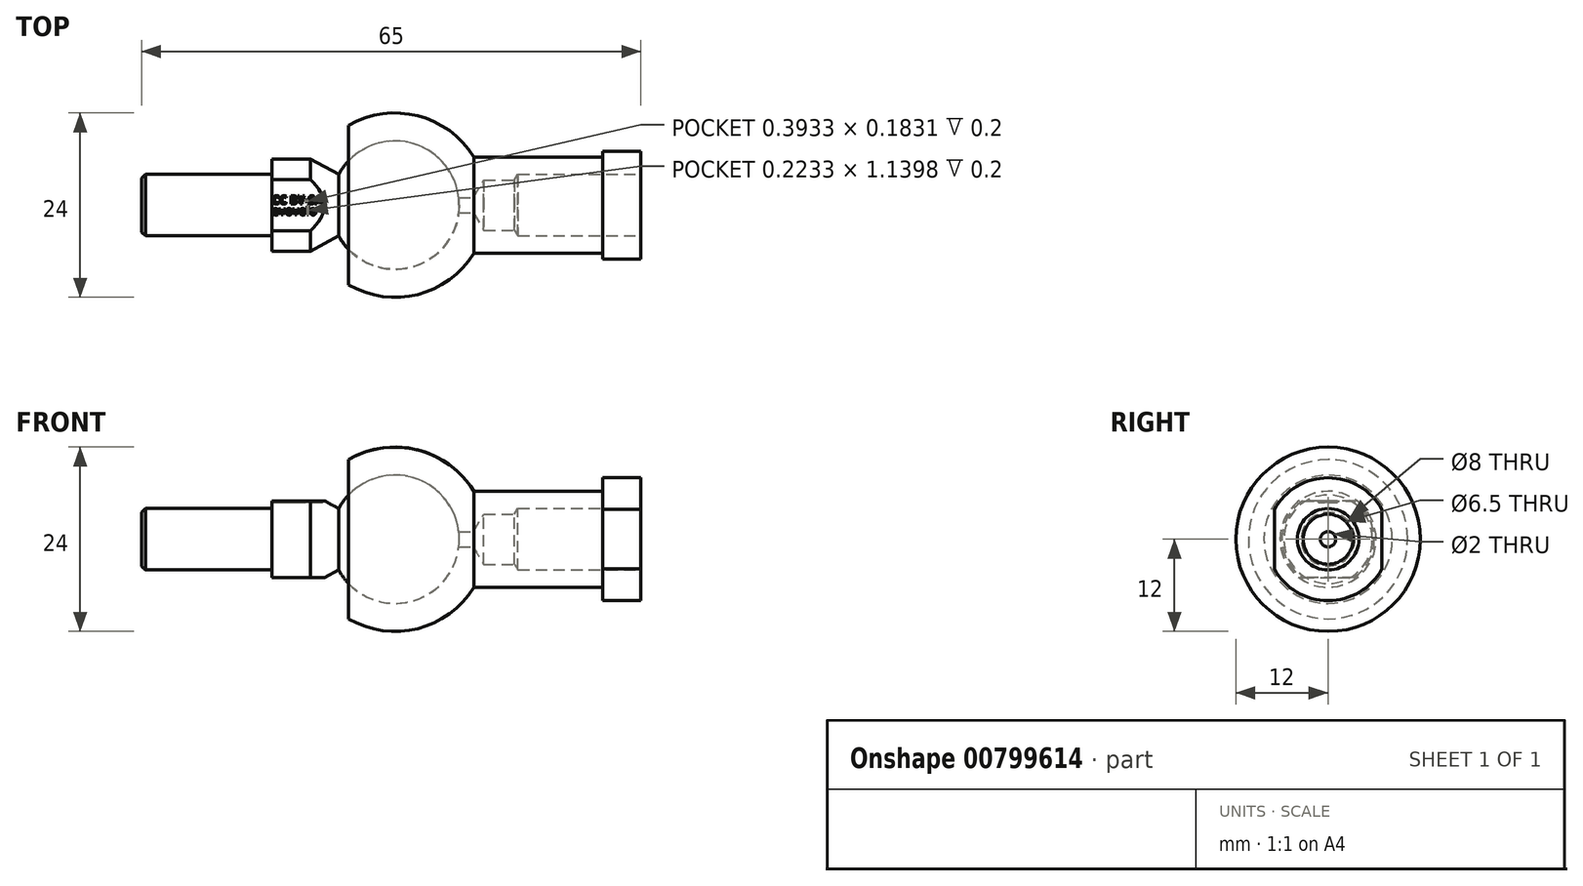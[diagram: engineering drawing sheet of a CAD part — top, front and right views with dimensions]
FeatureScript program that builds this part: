
annotation { "Feature Type Name" : "Feature", "Feature Type Description" : "" }
export const myFeature = defineFeature(function(context is Context, id is Id, definition is map)
    precondition{}
    {
        {
            var Q0;
            Q0=qCreatedBy(makeId("Top.planeOp"),FACE);
            var sketch = newSketch(context, id + "F0", { "sketchPlane" : qUnion([Q0])});
            skArc(sketch, "E0", {"start": v(8.35, 0) * mm, "mid": v(2.06, 8.1) * mm, "end": v(-7.33, 4) * mm});
            skArc(sketch, "E1", {"start": v(10.24, 6.25) * mm, "mid": v(2.94, 11.63) * mm, "end": v(-6.04, 10.37) * mm});
            skLineSegment(sketch, "E2", {"start": v(-42.01, 0) * mm, "end": v(52.59, 0) * mm, "construction": true});
            skLineSegment(sketch, "E3", {"start": v(10.24, 6.25) * mm, "end": v(27, 6.25) * mm});
            skLineSegment(sketch, "E4", {"start": v(27, 6.25) * mm, "end": v(27, 8) * mm});
            skLineSegment(sketch, "E5", {"start": v(27, 8) * mm, "end": v(32, 8) * mm});
            skLineSegment(sketch, "E6", {"start": v(32, 8) * mm, "end": v(32, 0) * mm});
            skLineSegment(sketch, "E7", {"start": v(32, 0) * mm, "end": v(8.35, 0) * mm});
            skLineSegment(sketch, "E8", {"start": v(0, 0) * mm, "end": v(-7.33, 4) * mm, "construction": true});
            skLineSegment(sketch, "E9", {"start": v(0, 0) * mm, "end": v(-6.04, 5.76) * mm, "construction": true});
            skLineSegment(sketch, "E10", {"start": v(-6.04, 10.37) * mm, "end": v(-6.04, 5.76) * mm});
            skLineSegment(sketch, "E11", {"start": v(0, 23.03) * mm, "end": v(0, -15.14) * mm, "construction": true});
            skLineSegment(sketch, "E12", {"start": v(-7.33, 4) * mm, "end": v(-11, 6) * mm});
            skLineSegment(sketch, "E13", {"start": v(-11, 6) * mm, "end": v(-16, 6) * mm});
            skLineSegment(sketch, "E14", {"start": v(-16, 6) * mm, "end": v(-16, 4) * mm});
            skLineSegment(sketch, "E15", {"start": v(-16, 4) * mm, "end": v(-33, 4) * mm});
            skLineSegment(sketch, "E16", {"start": v(-33, 4) * mm, "end": v(-33, 0) * mm});
            skLineSegment(sketch, "E17", {"start": v(-33, 0) * mm, "end": v(8.35, 0) * mm});
            skSolve(sketch);
        }
        {
            var Q0;
            Q0=makeQuery(id+"F0.imprint","IMPRINT",FACE,{"disambiguationData":[TD([[makeQuery(id+"F0.imprint","IMPRINT",EDGE,{"derivedFrom":sQuery(id+"F0.wireOp",EDGE,"E1")}),1.0]])]});
            var Q1;
            Q1=sQuery(id+"F0.wireOp",EDGE,"E2");
            revolve(context, id + "F1", {"entities" : qUnion([Q0]), "axis" : qUnion([Q1]), "revolveType" : RevolveType.FULL});
        }
        {
            var Q0;
            {var subQ1=sQuery(id+"F0.wireOp",EDGE,"E12");Q0=makeQuery(id+"F0.imprint","IMPRINT",FACE,{"disambiguationData":[TD([[makeQuery(id+"F0.imprint","IMPRINT",EDGE,{"derivedFrom":subQ1}),1.0]])]});}
            var Q1;
            Q1=sQuery(id+"F0.wireOp",EDGE,"E2");
            revolve(context, id + "F2", {"entities" : qUnion([Q0]), "axis" : qUnion([Q1]), "revolveType" : RevolveType.FULL});
        }
        {
            var Q0;
            Q0=makeQuery(id+"F1.opRevolve","SWEPT_FACE",FACE,{"disambiguationData":[OSD([sQuery(id+"F0.wireOp",EDGE,"E6")])]});
            var sketch = newSketch(context, id + "F3", { "sketchPlane" : qUnion([Q0])});
            skPoint(sketch, "E18", {"position": v(0, 0) * mm});
            skLineSegment(sketch, "E19", {"start": v(-7, 3.87) * mm, "end": v(-7, -3.87) * mm});
            skLineSegment(sketch, "E20", {"start": v(0, 12.06) * mm, "end": v(0, -11.37) * mm, "construction": true});
            skLineSegment(sketch, "E21.MirrorCS", {"start": v(7, 3.87) * mm, "end": v(7, -3.87) * mm});
            skSolve(sketch);
        }
        {
            var Q0;
            {var subQ1=sQuery(id+"F3.wireOp",EDGE,"E21.MirrorCS");Q0=makeQuery(id+"F3.imprint","IMPRINT",FACE,{"disambiguationData":[TD([[makeQuery(id+"F3.imprint","IMPRINT",EDGE,{"derivedFrom":subQ1}),1.0]])]});}
            var Q1;
            {var subQ1=sQuery(id+"F3.wireOp",EDGE,"E19");Q1=makeQuery(id+"F3.imprint","IMPRINT",FACE,{"disambiguationData":[TD([[makeQuery(id+"F3.imprint","IMPRINT",EDGE,{"derivedFrom":subQ1}),-1.0]])]});}
            extrude(context, id + "F4", {"entities" : qUnion([Q0, Q1]), "operationType" : NewBodyOperationType.REMOVE, "endBound" : BoundingType.UP_TO_NEXT, "oppositeDirection" : true, "depth" : 10 * mm});
        }
        {
            var Q0;
            Q0=sQuery(id+"F3.wireOp",VERTEX,"E18");
            var Q1;
            Q1=makeQuery(id+"F1.opRevolve","SWEPT_BODY",BODY,{"disambiguationData":[OSD([sQuery(id+"F0.wireOp",EDGE,"E0"),sQuery(id+"F0.wireOp",EDGE,"E1"),sQuery(id+"F0.wireOp",EDGE,"E3"),sQuery(id+"F0.wireOp",EDGE,"E4"),sQuery(id+"F0.wireOp",EDGE,"E5"),sQuery(id+"F0.wireOp",EDGE,"E6"),sQuery(id+"F0.wireOp",EDGE,"E7"),sQuery(id+"F0.wireOp",EDGE,"E10")])]});
            hole(context, id + "F5", {"style" : HoleStyle.SIMPLE, "holeDiameter" : 8 * mm, "endStyle" : HoleEndStyle.BLIND, "holeDepth" : 16 * mm, "locations" : qUnion([Q0]), "scope" : qUnion([Q1])});
        }
        {
            var Q0;
            Q0=sQuery(id+"F3.wireOp",VERTEX,"E18");
            var Q1;
            Q1=makeQuery(id+"F1.opRevolve","SWEPT_BODY",BODY,{"disambiguationData":[OSD([sQuery(id+"F0.wireOp",EDGE,"E0"),sQuery(id+"F0.wireOp",EDGE,"E1"),sQuery(id+"F0.wireOp",EDGE,"E3"),sQuery(id+"F0.wireOp",EDGE,"E4"),sQuery(id+"F0.wireOp",EDGE,"E5"),sQuery(id+"F0.wireOp",EDGE,"E6"),sQuery(id+"F0.wireOp",EDGE,"E7"),sQuery(id+"F0.wireOp",EDGE,"E10")])]});
            hole(context, id + "F6", {"style" : HoleStyle.SIMPLE, "holeDiameter" : 6.5 * mm, "endStyle" : HoleEndStyle.BLIND, "holeDepth" : 4 * mm, "locations" : qUnion([Q0]), "scope" : qUnion([Q1])});
        }
        {
            var Q0;
            Q0=sQuery(id+"F3.wireOp",VERTEX,"E18");
            var Q1;
            Q1=makeQuery(id+"F1.opRevolve","SWEPT_BODY",BODY,{"disambiguationData":[OSD([sQuery(id+"F0.wireOp",EDGE,"E0"),sQuery(id+"F0.wireOp",EDGE,"E1"),sQuery(id+"F0.wireOp",EDGE,"E3"),sQuery(id+"F0.wireOp",EDGE,"E4"),sQuery(id+"F0.wireOp",EDGE,"E5"),sQuery(id+"F0.wireOp",EDGE,"E6"),sQuery(id+"F0.wireOp",EDGE,"E7"),sQuery(id+"F0.wireOp",EDGE,"E10")])]});
            hole(context, id + "F7", {"style" : HoleStyle.SIMPLE, "holeDiameter" : 2 * mm, "endStyle" : HoleEndStyle.THROUGH, "locations" : qUnion([Q0]), "scope" : qUnion([Q1])});
        }
        {
            var Q0;
            Q0=makeQuery(id+"F2.opRevolve","SWEPT_FACE",FACE,{"disambiguationData":[OSD([sQuery(id+"F0.wireOp",EDGE,"E14")])]});
            var sketch = newSketch(context, id + "F8", { "sketchPlane" : qUnion([Q0])});
            skLineSegment(sketch, "E22", {"start": v(-3.32, 5) * mm, "end": v(3.32, 5) * mm});
            skLineSegment(sketch, "E23", {"start": v(-8.03, 0) * mm, "end": v(8.05, 0) * mm, "construction": true});
            skPoint(sketch, "E24.orphan", {"position": v(0, 0) * mm});
            skLineSegment(sketch, "E25.MirrorCS", {"start": v(-3.32, -5) * mm, "end": v(3.32, -5) * mm});
            skSolve(sketch);
        }
        {
            var Q0;
            {var subQ1=sQuery(id+"F8.wireOp",EDGE,"E22");Q0=makeQuery(id+"F8.imprint","IMPRINT",FACE,{"disambiguationData":[TD([[makeQuery(id+"F8.imprint","IMPRINT",EDGE,{"derivedFrom":subQ1}),1.0]])]});}
            var Q1;
            {var subQ1=sQuery(id+"F8.wireOp",EDGE,"E25.MirrorCS");Q1=makeQuery(id+"F8.imprint","IMPRINT",FACE,{"disambiguationData":[TD([[makeQuery(id+"F8.imprint","IMPRINT",EDGE,{"derivedFrom":subQ1}),-1.0]])]});}
            extrude(context, id + "F9", {"entities" : qUnion([Q0, Q1]), "operationType" : NewBodyOperationType.REMOVE, "endBound" : BoundingType.UP_TO_NEXT, "oppositeDirection" : true, "depth" : 25 * mm});
        }
        {
            var Q0;
            Q0=makeQuery(id+"F5.hole-0.boolean.opBoolean","COPY",EDGE,{"derivedFrom":makeQuery(id+"F5.hole-0.opRevolve","SWEPT_EDGE",EDGE,{"disambiguationData":[OSD([sQuery(id+"F5.hole-0.sketch.wireOp",EDGE,"core_line_2"),sQuery(id+"F5.hole-0.sketch.wireOp",EDGE,"core_line_3")])]})});
            var Q1;
            Q1=makeQuery(id+"F2.opRevolve","SWEPT_EDGE",EDGE,{"disambiguationData":[OSD([sQuery(id+"F0.wireOp",EDGE,"E15"),sQuery(id+"F0.wireOp",EDGE,"E16")])]});
            chamfer(context, id + "F10", {"entities" : qUnion([Q0, Q1]), "width" : 0.5 * mm, "tangentPropagation" : true});
        }
        {
            var Q0;
            Q0=makeQuery(id+"F9.boolean.opBoolean","COPY",FACE,{"derivedFrom":makeQuery(id+"F9.opExtrude","SWEPT_FACE",FACE,{"disambiguationData":[OSD([sQuery(id+"F8.wireOp",EDGE,"E22")])]})});
            var sketch = newSketch(context, id + "F11", { "sketchPlane" : qUnion([Q0])});
            skText(sketch, "E26", { "text": "CC BY-SA", "fontName": "OpenSans-Bold.ttf"});
            skText(sketch, "E27", { "text": "evovelo", "fontName": "OpenSans-Bold.ttf"});
            const initialGuessF11  = {"E26": [-0.016, 0.00015, 1, 0, 0.00108], "E27": [-0.016, -0.00127, 1, 0, 0.00108]};
            skSetInitialGuess(sketch, initialGuessF11);
            skSolve(sketch);
        }
        {
            var Q0;
            Q0=qSketchRegion(id+"F11",true);
            extrude(context, id + "F12", {"entities" : qUnion([Q0]), "operationType" : NewBodyOperationType.REMOVE, "oppositeDirection" : true, "depth" : 0.2 * mm});
        }
    });
